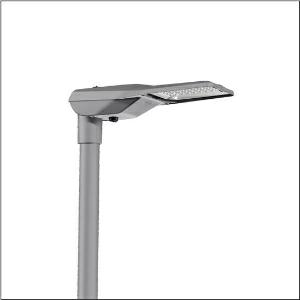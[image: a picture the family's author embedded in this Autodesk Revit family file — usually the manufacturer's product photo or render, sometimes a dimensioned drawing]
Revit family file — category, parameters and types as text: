
# Revit family: streetlight_sl_21_iq_mini___pl52_5xe2h31y08gb_067c
name_source: partatom
category: Lighting Fixtures
units: mm (PartAtom-declared; Revit-internal decimal feet)

## family parameters
Cut with Voids When Loaded = No
Host = Face
Light Source = No
Part Type = Normal
Room Calculation Point = No
Round Connector Dimension = Use Diameter
Shared = No

## types (1)
- --- (1 x LED, 5880 lm, 39.8 W, 3000K)
    Apparent Load = 40 VA
    CIE Flux Codes = 27 59 98 100 100
    Color Rendering = 70
    Color Temperature = 3000K
    Default Elevation = 1800 mm
    Description = Streetlight SL 21 iQ mini, mast luminaire, primary light control with lens, of PMMA, primary optical cover: cover, of toughened safety glass, transparent, light distribution: PL52, light emission: direct distribution, primary light characteristic: asymmetric, installation type: post-top, side-entry, LED, High Power LED, rated luminous flux: 5.880lm, luminous efficacy: 148lm/W, light colour: 730, colour temperature: 3000K, control: presetting dimming logarithmic, Street-Remote, Auto-Match, Temp-Guard, Lumen-Switch, Night-Set, Smart-Wire, Light-Fading, Desk-Remote (wireless, voltage-free reading and setting of iQ features in the workshop via application-optimized NFC function/RFID function), optimised constant luminous flux control (CLO 2.0), mains connection: 220..240V, AC, 50/60Hz, start of lifetime: 40W, end of service life: 41W, reduction: 18W, luminaire housing, of diecast aluminium, powder-coated, Siteco® metallic grey (DB 702S), corrosivity category C5 mid according to DIN EN ISO 12944, please order mast flange separately, inclination adjustable: 0°, 5°, 10°, 15°, sealing non-destructively replaceable, multi-level sealing system, length: 628mm, width: 235mm, height: 110mm, mast flange for spigot size: 42mm (side-entry): 5XC10008XM4, 60/48mm (side-entry/post-top): 5XC10108XM2, 76/60mm (side-entry/post-top): 5XC10108XM1, Smart Interface below and above, protection rating (complete): IP66, insulation class (complete): insulation class II (safety insulation), certification: CE, ENEC, ENEC+, VDE, impact resistance: IK09, permissible operating ambient temperature for outdoor applications: -40..+50°C, standard-compliant lighting for roads and squares, packaging unit: 1 piece

Light Distribution: PL52
    Height = 110 mm
    Lamp = 1 x LED
    Lamp Light Flux = 5880 lm
    Lamp Power = 39.8 W
    Lamp count = 1
    Length = 625 mm
    Luminous efficacy = 148 lm/W
    Manufacturer = Siteco
    ModVariant = No
    Model = 5XE2H31Y08GB
    Number of Poles = 1
    OnlyDefault = Yes
    Power Factor = 1
    Product Name = Streetlight SL 21 iQ mini | PL52
    Product group = mast luminaire | pylon top
    ProductGroupID = 6100
    Protection Class = Protection class II
    Protection Degree = IP 66
    RLX_Detail_Level = 1
    RLX_Emergency_Light_Flux = 0 lm
    RLX_Emergency_Type = 0
    RLX_Emergency_Type_DB = No
    RlxData = <blob elided: 102601 chars, md5=62986889>
    Socket = socket
    Standby Power = 0 W
    System Light Flux = 5880 lm
    System Power = 40 W
    Type Comments = factory setting: luminous flux: 100 % | dim-lin: 254 | 800 mA
    Type Image = l_1003514.jpg
    URL = http://relux.com
    VarID = @adj_045989
    Voltage = 0 V
    Weight = 0.00 kg
    Width = 234 mm

## geometry (parser evidence)
native form markers: Blend x4, Sweep x9
no freeform markers — native parametric forms only
